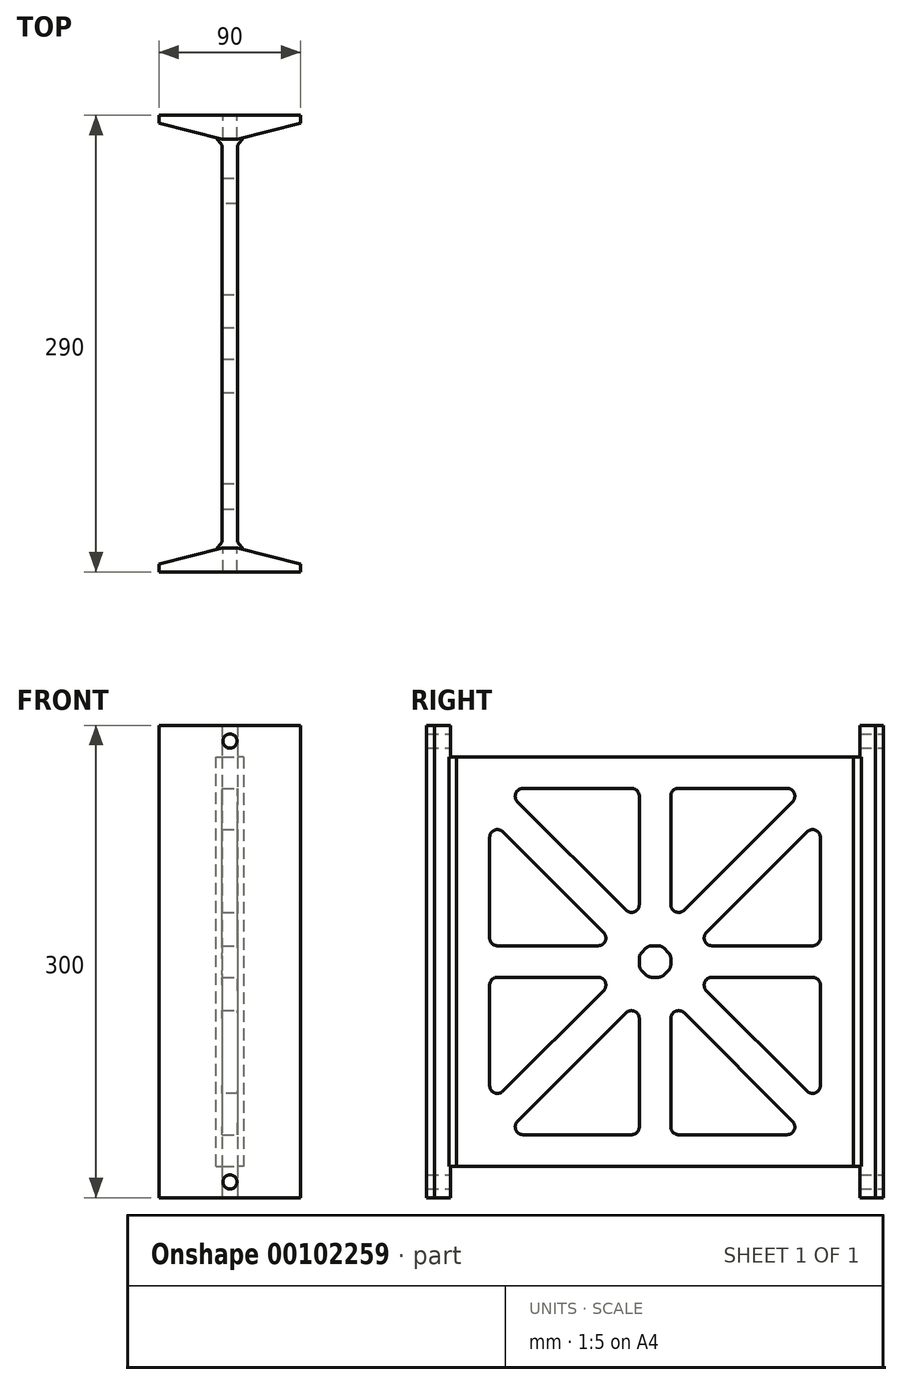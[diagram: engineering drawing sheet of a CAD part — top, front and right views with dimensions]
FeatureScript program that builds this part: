
annotation { "Feature Type Name" : "Feature", "Feature Type Description" : "" }
export const myFeature = defineFeature(function(context is Context, id is Id, definition is map)
    precondition{}
    {
        {
            var Q0;
            Q0=qCreatedBy(makeId("Top.planeOp"),FACE);
            var sketch = newSketch(context, id + "F0", { "sketchPlane" : qUnion([Q0])});
            skLineSegment(sketch, "E0", {"start": v(0, 290) * mm, "end": v(0, 285) * mm});
            skLineSegment(sketch, "E1", {"start": v(0, 5) * mm, "end": v(0, 0) * mm});
            skLineSegment(sketch, "E2", {"start": v(40, 15) * mm, "end": v(0, 5) * mm});
            skLineSegment(sketch, "E3", {"start": v(0, 290) * mm, "end": v(45, 290) * mm});
            skLineSegment(sketch, "E4", {"start": v(0, 0) * mm, "end": v(45, 0) * mm});
            skLineSegment(sketch, "E5", {"start": v(40, 275) * mm, "end": v(0, 285) * mm});
            skLineSegment(sketch, "E6", {"start": v(45, 290) * mm, "end": v(45, 0) * mm, "construction": true});
            skLineSegment(sketch, "E7.MirrorCS", {"start": v(90, 290) * mm, "end": v(45, 290) * mm});
            skLineSegment(sketch, "E8.MirrorCS", {"start": v(90, 290) * mm, "end": v(90, 285) * mm});
            skLineSegment(sketch, "E9.MirrorCS", {"start": v(50, 275) * mm, "end": v(90, 285) * mm});
            skLineSegment(sketch, "E10.MirrorCS", {"start": v(50, 15) * mm, "end": v(90, 5) * mm});
            skLineSegment(sketch, "E11.MirrorCS", {"start": v(90, 0) * mm, "end": v(45, 0) * mm});
            skLineSegment(sketch, "E12.MirrorCS", {"start": v(90, 5) * mm, "end": v(90, 0) * mm});
            skLineSegment(sketch, "E13", {"start": v(40, 275) * mm, "end": v(50, 275) * mm});
            skLineSegment(sketch, "E14", {"start": v(40, 15) * mm, "end": v(50, 15) * mm});
            skLineSegment(sketch, "E15", {"start": v(50, 15) * mm, "end": v(50, 275) * mm});
            skLineSegment(sketch, "E16", {"start": v(40, 275) * mm, "end": v(40, 15) * mm});
            skSolve(sketch);
        }
        {
            var Q0;
            Q0=makeQuery(id+"F0.imprint","IMPRINT",FACE,{"disambiguationData":[TD([[makeQuery(id+"F0.imprint","IMPRINT",EDGE,{"derivedFrom":sQuery(id+"F0.wireOp",EDGE,"E13")}),-1.0]])]});
            extrude(context, id + "F1", {"entities" : qUnion([Q0]), "depth" : 280 * mm, "hasSecondDirection" : true, "secondDirectionOppositeDirection" : false, "secondDirectionDepth" : 20 * mm});
        }
        {
            var Q0;
            Q0=makeQuery(id+"F0.imprint","IMPRINT",FACE,{"disambiguationData":[TD([[makeQuery(id+"F0.imprint","IMPRINT",EDGE,{"derivedFrom":sQuery(id+"F0.wireOp",EDGE,"E0")}),1.0]])]});
            var Q1;
            Q1=makeQuery(id+"F0.imprint","IMPRINT",FACE,{"disambiguationData":[TD([[makeQuery(id+"F0.imprint","IMPRINT",EDGE,{"derivedFrom":sQuery(id+"F0.wireOp",EDGE,"E1")}),1.0]])]});
            extrude(context, id + "F2", {"entities" : qUnion([Q0, Q1]), "operationType" : NewBodyOperationType.ADD, "depth" : 300 * mm});
        }
        {
            var Q0;
            {var subQ0=sQuery(id+"F0.wireOp",EDGE,"E14");var subQ1=sQuery(id+"F0.wireOp",EDGE,"E10.MirrorCS");var subQ2=sQuery(id+"F0.wireOp",EDGE,"E2");Q0=makeQuery(id+"F2.boolean.opBoolean","SPLIT",FACE,{"disambiguationData":[TD([makeQuery(id+"F2.opExtrude","CAP_FACE",FACE,{"disambiguationData":[OSD([sQuery(id+"F0.wireOp",EDGE,"E1"),subQ2,sQuery(id+"F0.wireOp",EDGE,"E4"),subQ1,sQuery(id+"F0.wireOp",EDGE,"E11.MirrorCS"),sQuery(id+"F0.wireOp",EDGE,"E12.MirrorCS"),subQ0])],"isStart":false})])],"derivedFrom":makeQuery(id+"F2.opExtrude","SWEPT_FACE",FACE,{"disambiguationData":[OSD([subQ0])]})});}
            var sketch = newSketch(context, id + "F3", { "sketchPlane" : qUnion([Q0])});
            skLineSegment(sketch, "E17", {"start": v(-45, 300) * mm, "end": v(-45, 0) * mm, "construction": true});
            skCircle(sketch, "E18", {"center": v(-45, 290) * mm, "radius": 4.5 * mm});
            skCircle(sketch, "E19", {"center": v(-45, 10) * mm, "radius": 4.5 * mm});
            skSolve(sketch);
        }
        {
            var Q0;
            Q0=makeQuery(id+"F3.imprint","IMPRINT",FACE,{"disambiguationData":[TD([[makeQuery(id+"F3.imprint","IMPRINT",EDGE,{"derivedFrom":sQuery(id+"F3.wireOp",EDGE,"E18")}),1.0]])]});
            var Q1;
            Q1=makeQuery(id+"F3.imprint","IMPRINT",FACE,{"disambiguationData":[TD([[makeQuery(id+"F3.imprint","IMPRINT",EDGE,{"derivedFrom":sQuery(id+"F3.wireOp",EDGE,"E19")}),1.0]])]});
            extrude(context, id + "F4", {"entities" : qUnion([Q0, Q1]), "operationType" : NewBodyOperationType.REMOVE, "endBound" : BoundingType.THROUGH_ALL, "oppositeDirection" : true, "depth" : 25 * mm, "hasSecondDirection" : true, "secondDirectionBound" : SecondDirectionBoundingType.THROUGH_ALL, "secondDirectionOppositeDirection" : false, "secondDirectionDepth" : 25 * mm});
        }
        {
            var Q0;
            {var subQ0=sQuery(id+"F0.wireOp",EDGE,"E13");var subQ1=sQuery(id+"F0.wireOp",EDGE,"427f2919-ef22-4325-9d07-79979d0573053.MirrorCS");var subQ2=sQuery(id+"F0.wireOp",EDGE,"E9.MirrorCS");Q0=makeQuery(id+"F2.boolean.opBoolean","MERGE",EDGE,{"derivedFrom":[makeQuery(id+"F1.opExtrude","SWEPT_EDGE",EDGE,{"disambiguationData":[OSD([subQ2,subQ1,subQ0])]}),makeQuery(id+"F2.opExtrude","SWEPT_EDGE",EDGE,{"disambiguationData":[OSD([subQ2,subQ1,subQ0])]})]});}
            var Q1;
            {var subQ0=sQuery(id+"F0.wireOp",EDGE,"E13");var subQ1=sQuery(id+"F0.wireOp",EDGE,"E5");var subQ2=sQuery(id+"F0.wireOp",EDGE,"Jg4K5WWO-BJFd-yvZ4-IYCn-kp8GdJ5CTJap");Q1=makeQuery(id+"F2.boolean.opBoolean","MERGE",EDGE,{"derivedFrom":[makeQuery(id+"F1.opExtrude","SWEPT_EDGE",EDGE,{"disambiguationData":[OSD([subQ2,subQ1,subQ0])]}),makeQuery(id+"F2.opExtrude","SWEPT_EDGE",EDGE,{"disambiguationData":[OSD([subQ2,subQ1,subQ0])]})]});}
            var Q2;
            {var subQ0=sQuery(id+"F0.wireOp",EDGE,"E14");var subQ1=sQuery(id+"F0.wireOp",EDGE,"E2");var subQ2=sQuery(id+"F0.wireOp",EDGE,"vkhgXw4s-Oij9-4rpc-IuWL-W60lVU6054c8");Q2=makeQuery(id+"F2.boolean.opBoolean","MERGE",EDGE,{"derivedFrom":[makeQuery(id+"F1.opExtrude","SWEPT_EDGE",EDGE,{"disambiguationData":[OSD([subQ2,subQ1,subQ0])]}),makeQuery(id+"F2.opExtrude","SWEPT_EDGE",EDGE,{"disambiguationData":[OSD([subQ2,subQ1,subQ0])]})]});}
            var Q3;
            {var subQ0=sQuery(id+"F0.wireOp",EDGE,"E14");var subQ1=sQuery(id+"F0.wireOp",EDGE,"E10.MirrorCS");var subQ2=sQuery(id+"F0.wireOp",EDGE,"427f2919-ef22-4325-9d07-79979d0573056.MirrorCS");Q3=makeQuery(id+"F2.boolean.opBoolean","MERGE",EDGE,{"derivedFrom":[makeQuery(id+"F1.opExtrude","SWEPT_EDGE",EDGE,{"disambiguationData":[OSD([subQ2,subQ1,subQ0])]}),makeQuery(id+"F2.opExtrude","SWEPT_EDGE",EDGE,{"disambiguationData":[OSD([subQ2,subQ1,subQ0])]})]});}
            chamfer(context, id + "F5", {"entities" : qUnion([Q0, Q1, Q2, Q3]), "width" : 5 * mm, "tangentPropagation" : true});
        }
        {
            var Q0;
            Q0=makeQuery(id+"F1.opExtrude","SWEPT_FACE",FACE,{"disambiguationData":[OSD([sQuery(id+"F0.wireOp",EDGE,"E15")])]});
            var sketch = newSketch(context, id + "F6", { "sketchPlane" : qUnion([Q0])});
            skLineSegment(sketch, "E20", {"start": v(270, 150) * mm, "end": v(20, 150) * mm, "construction": true});
            skLineSegment(sketch, "E21", {"start": v(145, 280) * mm, "end": v(145, 20) * mm, "construction": true});
            skCircle(sketch, "E22.cCircle", {"center": v(145, 150) * mm, "radius": 24.14 * mm, "construction": true});
            skLineSegment(sketch, "E22.0", {"start": v(120.86, 140) * mm, "end": v(120.86, 160) * mm, "construction": true});
            skLineSegment(sketch, "E22.1", {"start": v(120.86, 160) * mm, "end": v(135, 174.14) * mm, "construction": true});
            skLineSegment(sketch, "E22.2", {"start": v(135, 174.14) * mm, "end": v(155, 174.14) * mm, "construction": true});
            skLineSegment(sketch, "E22.3", {"start": v(155, 174.14) * mm, "end": v(169.14, 160) * mm, "construction": true});
            skLineSegment(sketch, "E22.4", {"start": v(169.14, 160) * mm, "end": v(169.14, 140) * mm, "construction": true});
            skLineSegment(sketch, "E22.5", {"start": v(169.14, 140) * mm, "end": v(155, 125.86) * mm, "construction": true});
            skLineSegment(sketch, "E22.6", {"start": v(155, 125.86) * mm, "end": v(135, 125.86) * mm, "construction": true});
            skLineSegment(sketch, "E22.7", {"start": v(135, 125.86) * mm, "end": v(120.86, 140) * mm, "construction": true});
            skPoint(sketch, "E22.0.midPoint", {"position": v(120.86, 150) * mm});
            skLineSegment(sketch, "E23", {"start": v(120.86, 160) * mm, "end": v(20, 260.86) * mm});
            skLineSegment(sketch, "E24", {"start": v(135, 174.14) * mm, "end": v(29.14, 280) * mm});
            skLineSegment(sketch, "E25", {"start": v(135, 174.14) * mm, "end": v(135, 280) * mm});
            skLineSegment(sketch, "E26", {"start": v(155, 174.14) * mm, "end": v(155, 280) * mm});
            skLineSegment(sketch, "E27", {"start": v(155, 174.14) * mm, "end": v(260.86, 280) * mm});
            skLineSegment(sketch, "E28", {"start": v(169.14, 160) * mm, "end": v(270, 260.86) * mm});
            skLineSegment(sketch, "E29", {"start": v(169.14, 160) * mm, "end": v(270, 160) * mm});
            skLineSegment(sketch, "E30", {"start": v(169.14, 140) * mm, "end": v(270, 140) * mm});
            skLineSegment(sketch, "E31", {"start": v(169.14, 140) * mm, "end": v(270, 39.14) * mm});
            skLineSegment(sketch, "E32", {"start": v(155, 125.86) * mm, "end": v(260.86, 20) * mm});
            skLineSegment(sketch, "E33", {"start": v(155, 125.86) * mm, "end": v(155, 20) * mm});
            skLineSegment(sketch, "E34", {"start": v(135, 125.86) * mm, "end": v(135, 20) * mm});
            skLineSegment(sketch, "E35", {"start": v(135, 125.86) * mm, "end": v(29.14, 20) * mm});
            skLineSegment(sketch, "E36", {"start": v(120.86, 140) * mm, "end": v(20, 39.14) * mm});
            skLineSegment(sketch, "E37", {"start": v(120.86, 140) * mm, "end": v(20, 140) * mm});
            skLineSegment(sketch, "E38", {"start": v(120.86, 160) * mm, "end": v(20, 160) * mm});
            skLineSegment(sketch, "E39", {"start": v(270, 260) * mm, "end": v(20, 260) * mm});
            skLineSegment(sketch, "E40", {"start": v(250, 280) * mm, "end": v(250, 20) * mm});
            skLineSegment(sketch, "E41", {"start": v(270, 40) * mm, "end": v(20, 40) * mm});
            skLineSegment(sketch, "E42", {"start": v(40, 20) * mm, "end": v(40, 280) * mm});
            skCircle(sketch, "E43.cCircle", {"center": v(145, 150) * mm, "radius": 10 * mm, "construction": true});
            skLineSegment(sketch, "E43.0", {"start": v(155, 154.14) * mm, "end": v(155, 145.86) * mm});
            skLineSegment(sketch, "E43.1", {"start": v(155, 145.86) * mm, "end": v(149.14, 140) * mm});
            skLineSegment(sketch, "E43.2", {"start": v(149.14, 140) * mm, "end": v(140.86, 140) * mm});
            skLineSegment(sketch, "E43.3", {"start": v(140.86, 140) * mm, "end": v(135, 145.86) * mm});
            skLineSegment(sketch, "E43.4", {"start": v(135, 145.86) * mm, "end": v(135, 154.14) * mm});
            skLineSegment(sketch, "E43.5", {"start": v(135, 154.14) * mm, "end": v(140.86, 160) * mm});
            skLineSegment(sketch, "E43.6", {"start": v(140.86, 160) * mm, "end": v(149.14, 160) * mm});
            skLineSegment(sketch, "E43.7", {"start": v(149.14, 160) * mm, "end": v(155, 154.14) * mm});
            skPoint(sketch, "E43.0.midPoint", {"position": v(155, 150) * mm});
            skSolve(sketch);
        }
        {
            var Q0;
            {var subQ0=sQuery(id+"F6.wireOp",EDGE,"E25");var subQ1=sQuery(id+"F6.wireOp",EDGE,"E24");var subQ2=makeQuery(id+"F6.imprint","INTERSECT",VERTEX,{"derivedFrom":[subQ1,subQ0]});Q0=makeQuery(id+"F6.imprint","IMPRINT",FACE,{"disambiguationData":[TD([[makeQuery(id+"F6.imprint","IMPRINT",EDGE,{"disambiguationData":[TD([[subQ2,-1.0]])],"derivedFrom":subQ1}),-1.0]])]});}
            var Q1;
            {var subQ0=sQuery(id+"F6.wireOp",EDGE,"E27");var subQ1=sQuery(id+"F6.wireOp",EDGE,"E26");var subQ2=makeQuery(id+"F6.imprint","INTERSECT",VERTEX,{"derivedFrom":[subQ1,subQ0]});Q1=makeQuery(id+"F6.imprint","IMPRINT",FACE,{"disambiguationData":[TD([[makeQuery(id+"F6.imprint","IMPRINT",EDGE,{"disambiguationData":[TD([[subQ2,-1.0]])],"derivedFrom":subQ1}),-1.0]])]});}
            var Q2;
            {var subQ0=sQuery(id+"F6.wireOp",EDGE,"E29");var subQ1=sQuery(id+"F6.wireOp",EDGE,"E28");var subQ2=makeQuery(id+"F6.imprint","INTERSECT",VERTEX,{"derivedFrom":[subQ1,subQ0]});Q2=makeQuery(id+"F6.imprint","IMPRINT",FACE,{"disambiguationData":[TD([[makeQuery(id+"F6.imprint","IMPRINT",EDGE,{"disambiguationData":[TD([[subQ2,-1.0]])],"derivedFrom":subQ1}),-1.0]])]});}
            var Q3;
            {var subQ0=sQuery(id+"F6.wireOp",EDGE,"E31");var subQ1=sQuery(id+"F6.wireOp",EDGE,"E30");var subQ2=makeQuery(id+"F6.imprint","INTERSECT",VERTEX,{"derivedFrom":[subQ1,subQ0]});Q3=makeQuery(id+"F6.imprint","IMPRINT",FACE,{"disambiguationData":[TD([[makeQuery(id+"F6.imprint","IMPRINT",EDGE,{"disambiguationData":[TD([[subQ2,-1.0]])],"derivedFrom":subQ1}),-1.0]])]});}
            var Q4;
            {var subQ0=sQuery(id+"F6.wireOp",EDGE,"E33");var subQ1=sQuery(id+"F6.wireOp",EDGE,"E32");var subQ2=makeQuery(id+"F6.imprint","INTERSECT",VERTEX,{"derivedFrom":[subQ1,subQ0]});Q4=makeQuery(id+"F6.imprint","IMPRINT",FACE,{"disambiguationData":[TD([[makeQuery(id+"F6.imprint","IMPRINT",EDGE,{"disambiguationData":[TD([[subQ2,-1.0]])],"derivedFrom":subQ1}),-1.0]])]});}
            var Q5;
            {var subQ0=sQuery(id+"F6.wireOp",EDGE,"E35");var subQ1=sQuery(id+"F6.wireOp",EDGE,"E34");var subQ2=makeQuery(id+"F6.imprint","INTERSECT",VERTEX,{"derivedFrom":[subQ1,subQ0]});Q5=makeQuery(id+"F6.imprint","IMPRINT",FACE,{"disambiguationData":[TD([[makeQuery(id+"F6.imprint","IMPRINT",EDGE,{"disambiguationData":[TD([[subQ2,-1.0]])],"derivedFrom":subQ1}),-1.0]])]});}
            var Q6;
            {var subQ0=sQuery(id+"F6.wireOp",EDGE,"E37");var subQ1=sQuery(id+"F6.wireOp",EDGE,"E36");var subQ2=makeQuery(id+"F6.imprint","INTERSECT",VERTEX,{"derivedFrom":[subQ1,subQ0]});Q6=makeQuery(id+"F6.imprint","IMPRINT",FACE,{"disambiguationData":[TD([[makeQuery(id+"F6.imprint","IMPRINT",EDGE,{"disambiguationData":[TD([[subQ2,-1.0]])],"derivedFrom":subQ1}),-1.0]])]});}
            var Q7;
            {var subQ0=sQuery(id+"F6.wireOp",EDGE,"E38");var subQ1=sQuery(id+"F6.wireOp",EDGE,"E23");var subQ2=makeQuery(id+"F6.imprint","INTERSECT",VERTEX,{"derivedFrom":[subQ1,subQ0]});Q7=makeQuery(id+"F6.imprint","IMPRINT",FACE,{"disambiguationData":[TD([[makeQuery(id+"F6.imprint","IMPRINT",EDGE,{"disambiguationData":[TD([[subQ2,-1.0]])],"derivedFrom":subQ1}),1.0]])]});}
            var Q8;
            Q8=makeQuery(id+"F6.imprint","IMPRINT",FACE,{"disambiguationData":[TD([[makeQuery(id+"F6.imprint","IMPRINT",EDGE,{"derivedFrom":sQuery(id+"F6.wireOp",EDGE,"E43.0")}),-1.0]])]});
            extrude(context, id + "F7", {"entities" : qUnion([Q0, Q1, Q2, Q3, Q4, Q5, Q6, Q7, Q8]), "operationType" : NewBodyOperationType.REMOVE, "endBound" : BoundingType.THROUGH_ALL, "oppositeDirection" : true, "depth" : 25 * mm});
        }
        {
            var Q0;
            Q0=makeQuery(id+"F7.boolean.opBoolean","COPY",EDGE,{"derivedFrom":makeQuery(id+"F7.opExtrude","SWEPT_EDGE",EDGE,{"disambiguationData":[OSD([sQuery(id+"F6.wireOp",EDGE,"E27"),sQuery(id+"F6.wireOp",EDGE,"E39")])]})});
            var Q1;
            Q1=makeQuery(id+"F7.boolean.opBoolean","COPY",EDGE,{"derivedFrom":makeQuery(id+"F7.opExtrude","SWEPT_EDGE",EDGE,{"disambiguationData":[OSD([sQuery(id+"F6.wireOp",EDGE,"E26"),sQuery(id+"F6.wireOp",EDGE,"E39")])]})});
            var Q2;
            Q2=makeQuery(id+"F7.boolean.opBoolean","COPY",EDGE,{"derivedFrom":makeQuery(id+"F7.opExtrude","SWEPT_EDGE",EDGE,{"disambiguationData":[OSD([sQuery(id+"F6.wireOp",EDGE,"E26"),sQuery(id+"F6.wireOp",EDGE,"E27")])]})});
            var Q3;
            Q3=makeQuery(id+"F7.boolean.opBoolean","COPY",EDGE,{"derivedFrom":makeQuery(id+"F7.opExtrude","SWEPT_EDGE",EDGE,{"disambiguationData":[OSD([sQuery(id+"F6.wireOp",EDGE,"E28"),sQuery(id+"F6.wireOp",EDGE,"E40")])]})});
            var Q4;
            Q4=makeQuery(id+"F7.boolean.opBoolean","COPY",EDGE,{"derivedFrom":makeQuery(id+"F7.opExtrude","SWEPT_EDGE",EDGE,{"disambiguationData":[OSD([sQuery(id+"F6.wireOp",EDGE,"E29"),sQuery(id+"F6.wireOp",EDGE,"E40")])]})});
            var Q5;
            Q5=makeQuery(id+"F7.boolean.opBoolean","COPY",EDGE,{"derivedFrom":makeQuery(id+"F7.opExtrude","SWEPT_EDGE",EDGE,{"disambiguationData":[OSD([sQuery(id+"F6.wireOp",EDGE,"E28"),sQuery(id+"F6.wireOp",EDGE,"E29")])]})});
            var Q6;
            Q6=makeQuery(id+"F7.boolean.opBoolean","COPY",EDGE,{"derivedFrom":makeQuery(id+"F7.opExtrude","SWEPT_EDGE",EDGE,{"disambiguationData":[OSD([sQuery(id+"F6.wireOp",EDGE,"E30"),sQuery(id+"F6.wireOp",EDGE,"E40")])]})});
            var Q7;
            Q7=makeQuery(id+"F7.boolean.opBoolean","COPY",EDGE,{"derivedFrom":makeQuery(id+"F7.opExtrude","SWEPT_EDGE",EDGE,{"disambiguationData":[OSD([sQuery(id+"F6.wireOp",EDGE,"E31"),sQuery(id+"F6.wireOp",EDGE,"E40")])]})});
            var Q8;
            Q8=makeQuery(id+"F7.boolean.opBoolean","COPY",EDGE,{"derivedFrom":makeQuery(id+"F7.opExtrude","SWEPT_EDGE",EDGE,{"disambiguationData":[OSD([sQuery(id+"F6.wireOp",EDGE,"E30"),sQuery(id+"F6.wireOp",EDGE,"E31")])]})});
            var Q9;
            Q9=makeQuery(id+"F7.boolean.opBoolean","COPY",EDGE,{"derivedFrom":makeQuery(id+"F7.opExtrude","SWEPT_EDGE",EDGE,{"disambiguationData":[OSD([sQuery(id+"F6.wireOp",EDGE,"E32"),sQuery(id+"F6.wireOp",EDGE,"E33")])]})});
            var Q10;
            Q10=makeQuery(id+"F7.boolean.opBoolean","COPY",EDGE,{"derivedFrom":makeQuery(id+"F7.opExtrude","SWEPT_EDGE",EDGE,{"disambiguationData":[OSD([sQuery(id+"F6.wireOp",EDGE,"E32"),sQuery(id+"F6.wireOp",EDGE,"E41")])]})});
            var Q11;
            Q11=makeQuery(id+"F7.boolean.opBoolean","COPY",EDGE,{"derivedFrom":makeQuery(id+"F7.opExtrude","SWEPT_EDGE",EDGE,{"disambiguationData":[OSD([sQuery(id+"F6.wireOp",EDGE,"E33"),sQuery(id+"F6.wireOp",EDGE,"E41")])]})});
            var Q12;
            Q12=makeQuery(id+"F7.boolean.opBoolean","COPY",EDGE,{"derivedFrom":makeQuery(id+"F7.opExtrude","SWEPT_EDGE",EDGE,{"disambiguationData":[OSD([sQuery(id+"F6.wireOp",EDGE,"E34"),sQuery(id+"F6.wireOp",EDGE,"E35")])]})});
            var Q13;
            Q13=makeQuery(id+"F7.boolean.opBoolean","COPY",EDGE,{"derivedFrom":makeQuery(id+"F7.opExtrude","SWEPT_EDGE",EDGE,{"disambiguationData":[OSD([sQuery(id+"F6.wireOp",EDGE,"E34"),sQuery(id+"F6.wireOp",EDGE,"E41")])]})});
            var Q14;
            Q14=makeQuery(id+"F7.boolean.opBoolean","COPY",EDGE,{"derivedFrom":makeQuery(id+"F7.opExtrude","SWEPT_EDGE",EDGE,{"disambiguationData":[OSD([sQuery(id+"F6.wireOp",EDGE,"E35"),sQuery(id+"F6.wireOp",EDGE,"E41")])]})});
            var Q15;
            Q15=makeQuery(id+"F7.boolean.opBoolean","COPY",EDGE,{"derivedFrom":makeQuery(id+"F7.opExtrude","SWEPT_EDGE",EDGE,{"disambiguationData":[OSD([sQuery(id+"F6.wireOp",EDGE,"E36"),sQuery(id+"F6.wireOp",EDGE,"E42")])]})});
            var Q16;
            Q16=makeQuery(id+"F7.boolean.opBoolean","COPY",EDGE,{"derivedFrom":makeQuery(id+"F7.opExtrude","SWEPT_EDGE",EDGE,{"disambiguationData":[OSD([sQuery(id+"F6.wireOp",EDGE,"E37"),sQuery(id+"F6.wireOp",EDGE,"E42")])]})});
            var Q17;
            Q17=makeQuery(id+"F7.boolean.opBoolean","COPY",EDGE,{"derivedFrom":makeQuery(id+"F7.opExtrude","SWEPT_EDGE",EDGE,{"disambiguationData":[OSD([sQuery(id+"F6.wireOp",EDGE,"E36"),sQuery(id+"F6.wireOp",EDGE,"E37")])]})});
            var Q18;
            Q18=makeQuery(id+"F7.boolean.opBoolean","COPY",EDGE,{"derivedFrom":makeQuery(id+"F7.opExtrude","SWEPT_EDGE",EDGE,{"disambiguationData":[OSD([sQuery(id+"F6.wireOp",EDGE,"E38"),sQuery(id+"F6.wireOp",EDGE,"E42")])]})});
            var Q19;
            Q19=makeQuery(id+"F7.boolean.opBoolean","COPY",EDGE,{"derivedFrom":makeQuery(id+"F7.opExtrude","SWEPT_EDGE",EDGE,{"disambiguationData":[OSD([sQuery(id+"F6.wireOp",EDGE,"E23"),sQuery(id+"F6.wireOp",EDGE,"E42")])]})});
            var Q20;
            Q20=makeQuery(id+"F7.boolean.opBoolean","COPY",EDGE,{"derivedFrom":makeQuery(id+"F7.opExtrude","SWEPT_EDGE",EDGE,{"disambiguationData":[OSD([sQuery(id+"F6.wireOp",EDGE,"E23"),sQuery(id+"F6.wireOp",EDGE,"E38")])]})});
            var Q21;
            Q21=makeQuery(id+"F7.boolean.opBoolean","COPY",EDGE,{"derivedFrom":makeQuery(id+"F7.opExtrude","SWEPT_EDGE",EDGE,{"disambiguationData":[OSD([sQuery(id+"F6.wireOp",EDGE,"E24"),sQuery(id+"F6.wireOp",EDGE,"E25")])]})});
            var Q22;
            Q22=makeQuery(id+"F7.boolean.opBoolean","COPY",EDGE,{"derivedFrom":makeQuery(id+"F7.opExtrude","SWEPT_EDGE",EDGE,{"disambiguationData":[OSD([sQuery(id+"F6.wireOp",EDGE,"E24"),sQuery(id+"F6.wireOp",EDGE,"E39")])]})});
            var Q23;
            Q23=makeQuery(id+"F7.boolean.opBoolean","COPY",EDGE,{"derivedFrom":makeQuery(id+"F7.opExtrude","SWEPT_EDGE",EDGE,{"disambiguationData":[OSD([sQuery(id+"F6.wireOp",EDGE,"E25"),sQuery(id+"F6.wireOp",EDGE,"E39")])]})});
            var Q24;
            Q24=makeQuery(id+"F7.boolean.opBoolean","COPY",EDGE,{"derivedFrom":makeQuery(id+"F7.opExtrude","SWEPT_EDGE",EDGE,{"disambiguationData":[OSD([sQuery(id+"F6.wireOp",EDGE,"E43.3"),sQuery(id+"F6.wireOp",EDGE,"E43.4")])]})});
            var Q25;
            Q25=makeQuery(id+"F7.boolean.opBoolean","COPY",EDGE,{"derivedFrom":makeQuery(id+"F7.opExtrude","SWEPT_EDGE",EDGE,{"disambiguationData":[OSD([sQuery(id+"F6.wireOp",EDGE,"E43.4"),sQuery(id+"F6.wireOp",EDGE,"E43.5")])]})});
            var Q26;
            Q26=makeQuery(id+"F7.boolean.opBoolean","COPY",EDGE,{"derivedFrom":makeQuery(id+"F7.opExtrude","SWEPT_EDGE",EDGE,{"disambiguationData":[OSD([sQuery(id+"F6.wireOp",EDGE,"E43.5"),sQuery(id+"F6.wireOp",EDGE,"E43.6")])]})});
            var Q27;
            Q27=makeQuery(id+"F7.boolean.opBoolean","COPY",EDGE,{"derivedFrom":makeQuery(id+"F7.opExtrude","SWEPT_EDGE",EDGE,{"disambiguationData":[OSD([sQuery(id+"F6.wireOp",EDGE,"E43.6"),sQuery(id+"F6.wireOp",EDGE,"E43.7")])]})});
            var Q28;
            Q28=makeQuery(id+"F7.boolean.opBoolean","COPY",EDGE,{"derivedFrom":makeQuery(id+"F7.opExtrude","SWEPT_EDGE",EDGE,{"disambiguationData":[OSD([sQuery(id+"F6.wireOp",EDGE,"E43.0"),sQuery(id+"F6.wireOp",EDGE,"E43.7")])]})});
            var Q29;
            Q29=makeQuery(id+"F7.boolean.opBoolean","COPY",EDGE,{"derivedFrom":makeQuery(id+"F7.opExtrude","SWEPT_EDGE",EDGE,{"disambiguationData":[OSD([sQuery(id+"F6.wireOp",EDGE,"E43.0"),sQuery(id+"F6.wireOp",EDGE,"E43.1")])]})});
            var Q30;
            Q30=makeQuery(id+"F7.boolean.opBoolean","COPY",EDGE,{"derivedFrom":makeQuery(id+"F7.opExtrude","SWEPT_EDGE",EDGE,{"disambiguationData":[OSD([sQuery(id+"F6.wireOp",EDGE,"E43.1"),sQuery(id+"F6.wireOp",EDGE,"E43.2")])]})});
            var Q31;
            Q31=makeQuery(id+"F7.boolean.opBoolean","COPY",EDGE,{"derivedFrom":makeQuery(id+"F7.opExtrude","SWEPT_EDGE",EDGE,{"disambiguationData":[OSD([sQuery(id+"F6.wireOp",EDGE,"E43.2"),sQuery(id+"F6.wireOp",EDGE,"E43.3")])]})});
            fillet(context, id + "F8", {"entities" : qUnion([Q0, Q1, Q2, Q3, Q4, Q5, Q6, Q7, Q8, Q9, Q10, Q11, Q12, Q13, Q14, Q15, Q16, Q17, Q18, Q19, Q20, Q21, Q22, Q23, Q24, Q25, Q26, Q27, Q28, Q29, Q30, Q31]), "radius" : 5 * mm, "tangentPropagation" : true, "allowEdgeOverflow" : false});
        }
    });
